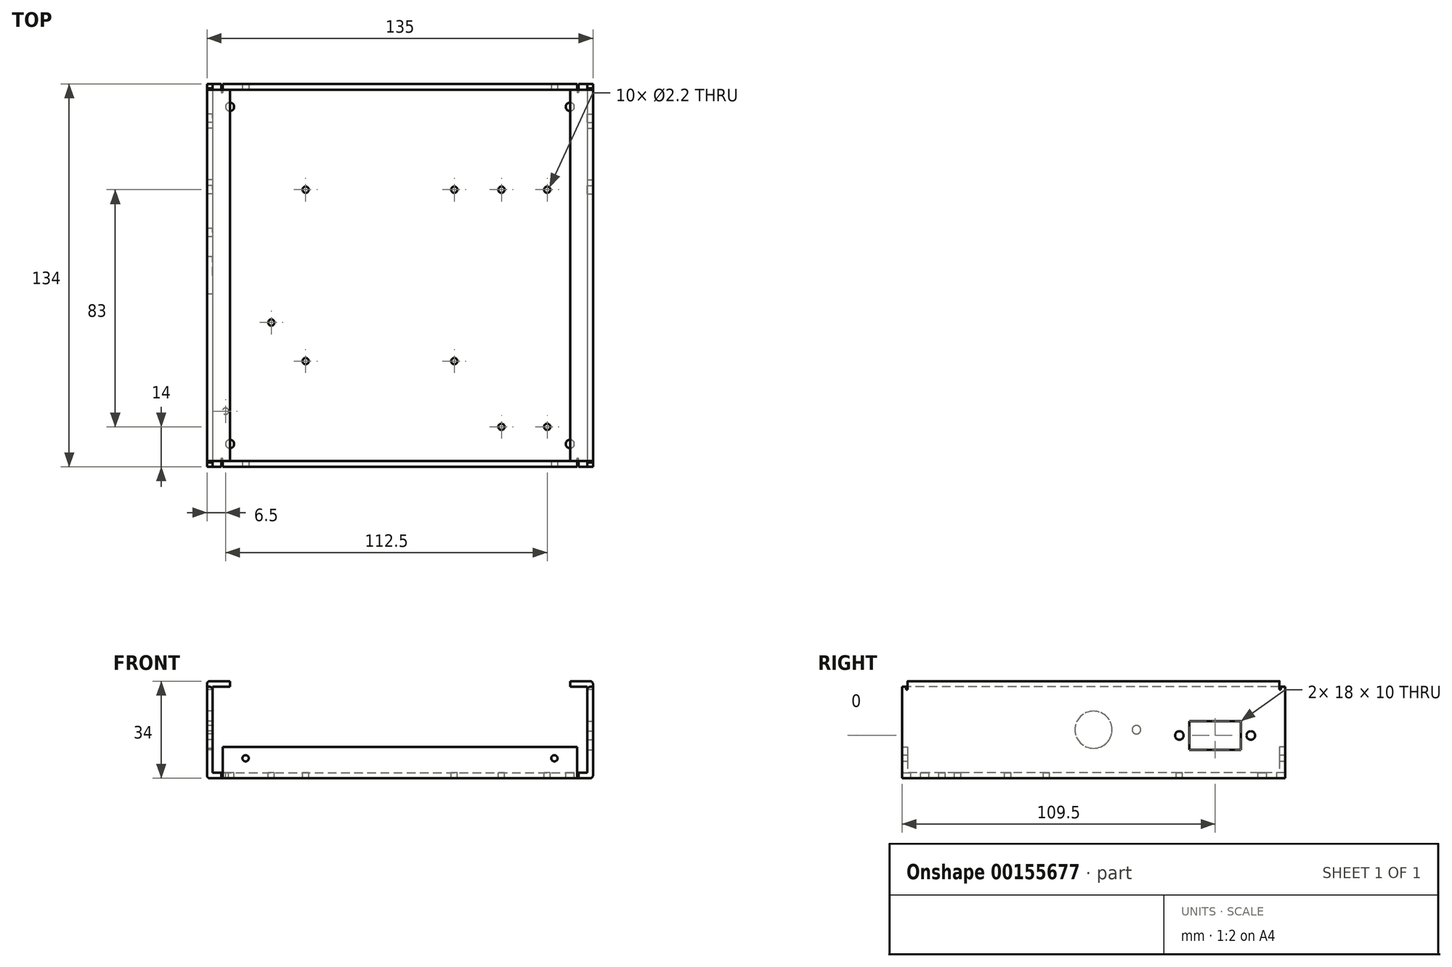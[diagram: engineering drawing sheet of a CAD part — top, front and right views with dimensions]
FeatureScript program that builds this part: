
annotation { "Feature Type Name" : "Feature", "Feature Type Description" : "" }
export const myFeature = defineFeature(function(context is Context, id is Id, definition is map)
    precondition{}
    {
        {
            var Q0;
            Q0=qCreatedBy(makeId("Top.planeOp"),FACE);
            var sketch = newSketch(context, id + "F0", { "sketchPlane" : qUnion([Q0])});
            skLineSegment(sketch, "E0.bottom", {"start": v(67.5, -67) * mm, "end": v(62.5, -67) * mm});
            skLineSegment(sketch, "E0.top", {"start": v(67.5, 67) * mm, "end": v(62.5, 67) * mm});
            skLineSegment(sketch, "E0.left", {"start": v(67.5, -67) * mm, "end": v(67.5, 67) * mm});
            skLineSegment(sketch, "E0.right", {"start": v(-67.5, -67) * mm, "end": v(-67.5, 67) * mm});
            skPoint(sketch, "E0.middle", {"position": v(0, 0) * mm});
            skLineSegment(sketch, "E1.top", {"start": v(-62.5, -64) * mm, "end": v(-62, -64) * mm});
            skLineSegment(sketch, "E1.left", {"start": v(-62.5, -67) * mm, "end": v(-62.5, -64) * mm});
            skLineSegment(sketch, "E1.right", {"start": v(-62, -67) * mm, "end": v(-62, -64) * mm});
            skLineSegment(sketch, "E2.trimOffspring", {"start": v(-62.5, -67) * mm, "end": v(-67.5, -67) * mm});
            skLineSegment(sketch, "E3.top", {"start": v(62, -64) * mm, "end": v(62.5, -64) * mm});
            skLineSegment(sketch, "E3.left", {"start": v(62, -67) * mm, "end": v(62, -64) * mm});
            skLineSegment(sketch, "E3.right", {"start": v(62.5, -67) * mm, "end": v(62.5, -64) * mm});
            skLineSegment(sketch, "E4.trimOffspring", {"start": v(62, -67) * mm, "end": v(-62, -67) * mm});
            skLineSegment(sketch, "E5.top", {"start": v(-62.5, 64) * mm, "end": v(-62, 64) * mm});
            skLineSegment(sketch, "E5.left", {"start": v(-62.5, 67) * mm, "end": v(-62.5, 64) * mm});
            skLineSegment(sketch, "E5.right", {"start": v(-62, 67) * mm, "end": v(-62, 64) * mm});
            skLineSegment(sketch, "E6.top", {"start": v(62.5, 64) * mm, "end": v(62, 64) * mm});
            skLineSegment(sketch, "E6.left", {"start": v(62.5, 67) * mm, "end": v(62.5, 64) * mm});
            skLineSegment(sketch, "E6.right", {"start": v(62, 67) * mm, "end": v(62, 64) * mm});
            skLineSegment(sketch, "E7.trimOffspring", {"start": v(-62.5, 67) * mm, "end": v(-67.5, 67) * mm});
            skLineSegment(sketch, "E8.trimOffspring", {"start": v(62, 67) * mm, "end": v(-62, 67) * mm});
            skSolve(sketch);
        }
        {
            var Q0;
            Q0 = qSketchRegion(id + "F0", true);
            extrude(context, id + "F1", {"entities" : qUnion([Q0]), "depth" : 2 * mm});
        }
        {
            var Q0;
            Q0=makeQuery(id+"F1.opExtrude","CAP_FACE",FACE,{"disambiguationData":[OSD([sQuery(id+"F0.wireOp",EDGE,"E0.bottom"),sQuery(id+"F0.wireOp",EDGE,"E0.top"),sQuery(id+"F0.wireOp",EDGE,"E0.left"),sQuery(id+"F0.wireOp",EDGE,"E0.right")])],"isStart":false});
            var sketch = newSketch(context, id + "F2", { "sketchPlane" : qUnion([Q0])});
            skLineSegment(sketch, "E9.bottom", {"start": v(67.5, 67) * mm, "end": v(65.5, 67) * mm});
            skLineSegment(sketch, "E9.top", {"start": v(67.5, -67) * mm, "end": v(65.5, -67) * mm});
            skLineSegment(sketch, "E9.left", {"start": v(67.5, 67) * mm, "end": v(67.5, -67) * mm});
            skLineSegment(sketch, "E9.right", {"start": v(65.5, 67) * mm, "end": v(65.5, -67) * mm});
            skLineSegment(sketch, "E10.bottom", {"start": v(-67.5, 67) * mm, "end": v(-65.5, 67) * mm});
            skLineSegment(sketch, "E10.top", {"start": v(-67.5, -67) * mm, "end": v(-65.5, -67) * mm});
            skLineSegment(sketch, "E10.left", {"start": v(-67.5, 67) * mm, "end": v(-67.5, -67) * mm});
            skLineSegment(sketch, "E10.right", {"start": v(-65.5, 67) * mm, "end": v(-65.5, -67) * mm});
            skSolve(sketch);
        }
        {
            var Q0;
            Q0 = qSketchRegion(id + "F2", true);
            extrude(context, id + "F3", {"entities" : qUnion([Q0]), "operationType" : NewBodyOperationType.ADD, "depth" : 30 * mm});
        }
        {
            var Q0;
            Q0=makeQuery(id+"F1.opExtrude","CAP_EDGE",EDGE,{"disambiguationData":[OSD([sQuery(id+"F0.wireOp",EDGE,"E0.right")])],"isStart":true});
            var Q1;
            Q1=makeQuery(id+"F1.opExtrude","CAP_EDGE",EDGE,{"disambiguationData":[OSD([sQuery(id+"F0.wireOp",EDGE,"E0.left")])],"isStart":true});
            var Q2;
            Q2=makeQuery(id+"F3.opExtrude","CAP_EDGE",EDGE,{"disambiguationData":[OSD([sQuery(id+"F2.wireOp",EDGE,"E10.right")])],"isStart":true});
            var Q3;
            Q3=makeQuery(id+"F3.opExtrude","CAP_EDGE",EDGE,{"disambiguationData":[OSD([sQuery(id+"F2.wireOp",EDGE,"E9.right")])],"isStart":true});
            fillet(context, id + "F4", {"entities" : qUnion([Q0, Q1, Q2, Q3]), "radius" : 1 * mm, "tangentPropagation" : true, "allowEdgeOverflow" : false});
        }
        {
            var Q0;
            Q0=makeQuery(id+"F3.opExtrude","CAP_FACE",FACE,{"disambiguationData":[OSD([sQuery(id+"F2.wireOp",EDGE,"E10.bottom"),sQuery(id+"F2.wireOp",EDGE,"E10.top"),sQuery(id+"F2.wireOp",EDGE,"E10.left"),sQuery(id+"F2.wireOp",EDGE,"E10.right")])],"isStart":false});
            var sketch = newSketch(context, id + "F5", { "sketchPlane" : qUnion([Q0])});
            skLineSegment(sketch, "E11.bottom", {"start": v(-67.5, 65) * mm, "end": v(-59.5, 65) * mm});
            skLineSegment(sketch, "E11.top", {"start": v(-67.5, -65) * mm, "end": v(-59.5, -65) * mm});
            skLineSegment(sketch, "E11.left", {"start": v(-67.5, 65) * mm, "end": v(-67.5, -65) * mm});
            skLineSegment(sketch, "E11.right", {"start": v(-59.5, 65) * mm, "end": v(-59.5, -65) * mm});
            skLineSegment(sketch, "E12.bottom", {"start": v(59.5, 65) * mm, "end": v(67.5, 65) * mm});
            skLineSegment(sketch, "E12.top", {"start": v(59.5, -65) * mm, "end": v(67.5, -65) * mm});
            skLineSegment(sketch, "E12.left", {"start": v(59.5, 65) * mm, "end": v(59.5, -65) * mm});
            skLineSegment(sketch, "E12.right", {"start": v(67.5, 65) * mm, "end": v(67.5, -65) * mm});
            skSolve(sketch);
        }
        {
            var Q0;
            Q0 = qSketchRegion(id + "F5", true);
            extrude(context, id + "F6", {"entities" : qUnion([Q0]), "operationType" : NewBodyOperationType.ADD, "depth" : 2 * mm});
        }
        {
            var Q0;
            Q0=makeQuery(id+"F6.opExtrude","CAP_EDGE",EDGE,{"disambiguationData":[OSD([sQuery(id+"F5.wireOp",EDGE,"E11.left")])],"isStart":false});
            var Q1;
            Q1=makeQuery(id+"F6.opExtrude","CAP_EDGE",EDGE,{"disambiguationData":[OSD([sQuery(id+"F5.wireOp",EDGE,"E12.right")])],"isStart":false});
            var Q2;
            {var subQ0=sQuery(id+"F5.wireOp",EDGE,"E11.top");var subQ1=sQuery(id+"F5.wireOp",EDGE,"E11.bottom");var subQ2=sQuery(id+"F2.wireOp",EDGE,"E10.right");Q2=makeQuery(id+"F6.boolean.opBoolean","SPLIT",EDGE,{"disambiguationData":[TD([makeQuery(id+"F3.opExtrude","CAP_FACE",FACE,{"disambiguationData":[OSD([sQuery(id+"F2.wireOp",EDGE,"E10.bottom"),sQuery(id+"F2.wireOp",EDGE,"E10.top"),sQuery(id+"F2.wireOp",EDGE,"E10.left"),subQ2])],"isStart":false}),makeQuery(id+"F3.opExtrude","SWEPT_FACE",FACE,{"disambiguationData":[OSD([subQ2])]}),makeQuery(id+"F6.opExtrude","SWEPT_FACE",FACE,{"disambiguationData":[OSD([subQ1])]}),makeQuery(id+"F6.opExtrude","CAP_FACE",FACE,{"disambiguationData":[OSD([subQ1,subQ0,sQuery(id+"F5.wireOp",EDGE,"E11.left"),sQuery(id+"F5.wireOp",EDGE,"E11.right")])],"isStart":true}),makeQuery(id+"F6.opExtrude","SWEPT_FACE",FACE,{"disambiguationData":[OSD([subQ0])]})])],"derivedFrom":makeQuery(id+"F3.opExtrude","CAP_EDGE",EDGE,{"disambiguationData":[OSD([subQ2])],"isStart":false})});}
            var Q3;
            {var subQ0=sQuery(id+"F5.wireOp",EDGE,"E12.top");var subQ1=sQuery(id+"F5.wireOp",EDGE,"E12.bottom");var subQ2=sQuery(id+"F2.wireOp",EDGE,"E9.right");Q3=makeQuery(id+"F6.boolean.opBoolean","SPLIT",EDGE,{"disambiguationData":[TD([makeQuery(id+"F3.opExtrude","CAP_FACE",FACE,{"disambiguationData":[OSD([sQuery(id+"F2.wireOp",EDGE,"E9.bottom"),sQuery(id+"F2.wireOp",EDGE,"E9.top"),sQuery(id+"F2.wireOp",EDGE,"E9.left"),subQ2])],"isStart":false}),makeQuery(id+"F3.opExtrude","SWEPT_FACE",FACE,{"disambiguationData":[OSD([subQ2])]}),makeQuery(id+"F6.opExtrude","SWEPT_FACE",FACE,{"disambiguationData":[OSD([subQ1])]}),makeQuery(id+"F6.opExtrude","CAP_FACE",FACE,{"disambiguationData":[OSD([subQ1,subQ0,sQuery(id+"F5.wireOp",EDGE,"E12.left"),sQuery(id+"F5.wireOp",EDGE,"E12.right")])],"isStart":true}),makeQuery(id+"F6.opExtrude","SWEPT_FACE",FACE,{"disambiguationData":[OSD([subQ0])]})])],"derivedFrom":makeQuery(id+"F3.opExtrude","CAP_EDGE",EDGE,{"disambiguationData":[OSD([subQ2])],"isStart":false})});}
            fillet(context, id + "F7", {"entities" : qUnion([Q0, Q1, Q2, Q3]), "radius" : 1 * mm, "tangentPropagation" : true, "allowEdgeOverflow" : false});
        }
        {
            var Q0;
            Q0=makeQuery(id+"F1.opExtrude","CAP_FACE",FACE,{"disambiguationData":[OSD([sQuery(id+"F0.wireOp",EDGE,"E0.bottom"),sQuery(id+"F0.wireOp",EDGE,"E0.top"),sQuery(id+"F0.wireOp",EDGE,"E0.left"),sQuery(id+"F0.wireOp",EDGE,"E0.right"),sQuery(id+"F0.wireOp",EDGE,"E1.top"),sQuery(id+"F0.wireOp",EDGE,"E1.left"),sQuery(id+"F0.wireOp",EDGE,"E1.right"),sQuery(id+"F0.wireOp",EDGE,"E2.trimOffspring"),sQuery(id+"F0.wireOp",EDGE,"E3.top"),sQuery(id+"F0.wireOp",EDGE,"E3.left"),sQuery(id+"F0.wireOp",EDGE,"E3.right"),sQuery(id+"F0.wireOp",EDGE,"E4.trimOffspring")])],"isStart":false});
            var sketch = newSketch(context, id + "F8", { "sketchPlane" : qUnion([Q0])});
            skLineSegment(sketch, "E13.bottom", {"start": v(-62, -65) * mm, "end": v(62, -65) * mm});
            skLineSegment(sketch, "E13.top", {"start": v(-62, -67) * mm, "end": v(62, -67) * mm});
            skLineSegment(sketch, "E13.left", {"start": v(-62, -65) * mm, "end": v(-62, -67) * mm});
            skLineSegment(sketch, "E13.right", {"start": v(62, -65) * mm, "end": v(62, -67) * mm});
            skLineSegment(sketch, "E14.bottom", {"start": v(-62, 67) * mm, "end": v(62, 67) * mm});
            skLineSegment(sketch, "E14.top", {"start": v(-62, 65) * mm, "end": v(62, 65) * mm});
            skLineSegment(sketch, "E14.left", {"start": v(-62, 67) * mm, "end": v(-62, 65) * mm});
            skLineSegment(sketch, "E14.right", {"start": v(62, 67) * mm, "end": v(62, 65) * mm});
            skSolve(sketch);
        }
        {
            var Q0;
            Q0 = qSketchRegion(id + "F8", true);
            extrude(context, id + "F9", {"entities" : qUnion([Q0]), "operationType" : NewBodyOperationType.ADD, "depth" : 9 * mm});
        }
        {
            var Q0;
            Q0=makeQuery(id+"F1.opExtrude","CAP_EDGE",EDGE,{"disambiguationData":[OSD([sQuery(id+"F0.wireOp",EDGE,"E4.trimOffspring")])],"isStart":true});
            var Q1;
            Q1=makeQuery(id+"F9.opExtrude","CAP_EDGE",EDGE,{"disambiguationData":[OSD([sQuery(id+"F8.wireOp",EDGE,"E13.bottom")])],"isStart":true});
            var Q2;
            Q2=makeQuery(id+"F9.opExtrude","CAP_EDGE",EDGE,{"disambiguationData":[OSD([sQuery(id+"F8.wireOp",EDGE,"E14.top")])],"isStart":true});
            var Q3;
            Q3=makeQuery(id+"F1.opExtrude","CAP_EDGE",EDGE,{"disambiguationData":[OSD([sQuery(id+"F0.wireOp",EDGE,"E8.trimOffspring")])],"isStart":true});
            fillet(context, id + "F10", {"entities" : qUnion([Q0, Q1, Q2, Q3]), "radius" : 1 * mm, "tangentPropagation" : true, "allowEdgeOverflow" : false});
        }
        {
            var Q0;
            Q0=makeQuery(id+"F6.boolean.opBoolean","MERGE",FACE,{"derivedFrom":[makeQuery(id+"F3.boolean.opBoolean","MERGE",FACE,{"derivedFrom":[makeQuery(id+"F1.opExtrude","SWEPT_FACE",FACE,{"disambiguationData":[OSD([sQuery(id+"F0.wireOp",EDGE,"E0.right")])]}),makeQuery(id+"F3.opExtrude","SWEPT_FACE",FACE,{"disambiguationData":[OSD([sQuery(id+"F2.wireOp",EDGE,"LtGDmYED-3yVl-KpR6-pZyB-YukeFVbaKuZ8.left")])]})]}),makeQuery(id+"F6.opExtrude","SWEPT_FACE",FACE,{"disambiguationData":[OSD([sQuery(id+"F5.wireOp",EDGE,"E11.left")])]})]});
            var sketch = newSketch(context, id + "F11", { "sketchPlane" : qUnion([Q0])});
            skLineSegment(sketch, "E15.bottom", {"start": v(65, 32) * mm, "end": v(65.5, 32) * mm});
            skLineSegment(sketch, "E15.top", {"start": v(65, 31) * mm, "end": v(65.5, 31) * mm});
            skLineSegment(sketch, "E15.left", {"start": v(65, 32) * mm, "end": v(65, 31) * mm});
            skLineSegment(sketch, "E15.right", {"start": v(65.5, 32) * mm, "end": v(65.5, 31) * mm});
            skLineSegment(sketch, "E16.bottom", {"start": v(-65, 32) * mm, "end": v(-65.5, 32) * mm});
            skLineSegment(sketch, "E16.top", {"start": v(-65, 31) * mm, "end": v(-65.5, 31) * mm});
            skLineSegment(sketch, "E16.left", {"start": v(-65, 32) * mm, "end": v(-65, 31) * mm});
            skLineSegment(sketch, "E16.right", {"start": v(-65.5, 32) * mm, "end": v(-65.5, 31) * mm});
            skSolve(sketch);
        }
        {
            var Q0;
            Q0 = qSketchRegion(id + "F11", true);
            extrude(context, id + "F12", {"entities" : qUnion([Q0]), "operationType" : NewBodyOperationType.REMOVE, "endBound" : BoundingType.THROUGH_ALL, "oppositeDirection" : true, "depth" : 25 * mm});
        }
        {
            var Q0;
            Q0=makeQuery(id+"F6.boolean.opBoolean","MERGE",FACE,{"derivedFrom":[makeQuery(id+"F3.boolean.opBoolean","MERGE",FACE,{"derivedFrom":[makeQuery(id+"F1.opExtrude","SWEPT_FACE",FACE,{"disambiguationData":[OSD([sQuery(id+"F0.wireOp",EDGE,"E0.right")])]}),makeQuery(id+"F3.opExtrude","SWEPT_FACE",FACE,{"disambiguationData":[OSD([sQuery(id+"F2.wireOp",EDGE,"E10.left")])]})]}),makeQuery(id+"F6.opExtrude","SWEPT_FACE",FACE,{"disambiguationData":[OSD([sQuery(id+"F5.wireOp",EDGE,"E11.left")])]})]});
            var sketch = newSketch(context, id + "F13", { "sketchPlane" : qUnion([Q0])});
            skCircle(sketch, "E17", {"center": v(-55, 15) * mm, "radius": 1.5 * mm});
            skCircle(sketch, "E18", {"center": v(-30, 15) * mm, "radius": 1.5 * mm});
            skCircle(sketch, "E19", {"center": v(0, 17) * mm, "radius": 6.5 * mm});
            skCircle(sketch, "E20", {"center": v(-15, 17) * mm, "radius": 1.5 * mm});
            skLineSegment(sketch, "E21.bottom", {"start": v(-33.5, 10) * mm, "end": v(-51.5, 10) * mm});
            skLineSegment(sketch, "E21.top", {"start": v(-33.5, 20) * mm, "end": v(-51.5, 20) * mm});
            skLineSegment(sketch, "E21.left", {"start": v(-33.5, 10) * mm, "end": v(-33.5, 20) * mm});
            skLineSegment(sketch, "E21.right", {"start": v(-51.5, 10) * mm, "end": v(-51.5, 20) * mm});
            skPoint(sketch, "E21.middle", {"position": v(-42.5, 15) * mm});
            skSolve(sketch);
        }
        {
            var Q0;
            Q0 = qSketchRegion(id + "F13", true);
            extrude(context, id + "F14", {"entities" : qUnion([Q0]), "operationType" : NewBodyOperationType.REMOVE, "oppositeDirection" : true, "depth" : 3 * mm});
        }
        {
            var Q0;
            Q0=makeQuery(id+"F1.opExtrude","CAP_FACE",FACE,{"disambiguationData":[OSD([sQuery(id+"F0.wireOp",EDGE,"E0.bottom"),sQuery(id+"F0.wireOp",EDGE,"E0.top"),sQuery(id+"F0.wireOp",EDGE,"E0.left"),sQuery(id+"F0.wireOp",EDGE,"E0.right"),sQuery(id+"F0.wireOp",EDGE,"E1.top"),sQuery(id+"F0.wireOp",EDGE,"E1.left"),sQuery(id+"F0.wireOp",EDGE,"E1.right"),sQuery(id+"F0.wireOp",EDGE,"E2.trimOffspring"),sQuery(id+"F0.wireOp",EDGE,"E3.top"),sQuery(id+"F0.wireOp",EDGE,"E3.left"),sQuery(id+"F0.wireOp",EDGE,"E3.right"),sQuery(id+"F0.wireOp",EDGE,"E4.trimOffspring"),sQuery(id+"F0.wireOp",EDGE,"E5.top"),sQuery(id+"F0.wireOp",EDGE,"E5.left"),sQuery(id+"F0.wireOp",EDGE,"E5.right"),sQuery(id+"F0.wireOp",EDGE,"E6.top"),sQuery(id+"F0.wireOp",EDGE,"E6.left"),sQuery(id+"F0.wireOp",EDGE,"E6.right"),sQuery(id+"F0.wireOp",EDGE,"E7.trimOffspring"),sQuery(id+"F0.wireOp",EDGE,"E8.trimOffspring")])],"isStart":false});
            var sketch = newSketch(context, id + "F15", { "sketchPlane" : qUnion([Q0])});
            skCircle(sketch, "E22", {"center": v(-33, 30) * mm, "radius": 1.1 * mm});
            skCircle(sketch, "E23", {"center": v(19, 30) * mm, "radius": 1.1 * mm});
            skCircle(sketch, "E24", {"center": v(-33, -30) * mm, "radius": 1.1 * mm});
            skCircle(sketch, "E25", {"center": v(19, -30) * mm, "radius": 1.1 * mm});
            skCircle(sketch, "E26", {"center": v(-45, -16.5) * mm, "radius": 1.1 * mm});
            skCircle(sketch, "E27", {"center": v(-61, -47.5) * mm, "radius": 1.1 * mm});
            skCircle(sketch, "E28", {"center": v(-59.5, 59) * mm, "radius": 1.5 * mm});
            skCircle(sketch, "E29", {"center": v(59.5, 59) * mm, "radius": 1.5 * mm});
            skCircle(sketch, "E30", {"center": v(-59.5, -59) * mm, "radius": 1.5 * mm});
            skCircle(sketch, "E31", {"center": v(59.5, -59) * mm, "radius": 1.5 * mm});
            skCircle(sketch, "E32", {"center": v(35.5, 30) * mm, "radius": 1.1 * mm});
            skCircle(sketch, "E33", {"center": v(51.5, 30) * mm, "radius": 1.1 * mm});
            skCircle(sketch, "E34", {"center": v(35.5, -53) * mm, "radius": 1.1 * mm});
            skCircle(sketch, "E35", {"center": v(51.5, -53) * mm, "radius": 1.1 * mm});
            skSolve(sketch);
        }
        {
            var Q0;
            Q0 = qSketchRegion(id + "F15", true);
            extrude(context, id + "F16", {"entities" : qUnion([Q0]), "operationType" : NewBodyOperationType.REMOVE, "oppositeDirection" : true, "depth" : 3 * mm});
        }
        {
            var Q0;
            Q0=makeQuery(id+"F9.boolean.opBoolean","MERGE",FACE,{"derivedFrom":[makeQuery(id+"F1.opExtrude","SWEPT_FACE",FACE,{"disambiguationData":[OSD([sQuery(id+"F0.wireOp",EDGE,"E4.trimOffspring")])]}),makeQuery(id+"F9.opExtrude","SWEPT_FACE",FACE,{"disambiguationData":[OSD([sQuery(id+"F8.wireOp",EDGE,"E13.top")])]})]});
            var sketch = newSketch(context, id + "F17", { "sketchPlane" : qUnion([Q0])});
            skCircle(sketch, "E36", {"center": v(54, 7) * mm, "radius": 1.1 * mm});
            skCircle(sketch, "E37", {"center": v(-54, 7) * mm, "radius": 1.1 * mm});
            skSolve(sketch);
        }
        {
            var Q0;
            Q0 = qSketchRegion(id + "F17", true);
            extrude(context, id + "F18", {"entities" : qUnion([Q0]), "operationType" : NewBodyOperationType.REMOVE, "endBound" : BoundingType.THROUGH_ALL, "oppositeDirection" : true, "depth" : 25 * mm});
        }
        {
            var Q0;
            Q0=makeQuery(id+"F6.boolean.opBoolean","MERGE",FACE,{"derivedFrom":[makeQuery(id+"F3.boolean.opBoolean","MERGE",FACE,{"derivedFrom":[makeQuery(id+"F1.opExtrude","SWEPT_FACE",FACE,{"disambiguationData":[OSD([sQuery(id+"F0.wireOp",EDGE,"E0.left")])]}),makeQuery(id+"F3.opExtrude","SWEPT_FACE",FACE,{"disambiguationData":[OSD([sQuery(id+"F2.wireOp",EDGE,"E9.left")])]})]}),makeQuery(id+"F6.opExtrude","SWEPT_FACE",FACE,{"disambiguationData":[OSD([sQuery(id+"F5.wireOp",EDGE,"E12.right")])]})]});
            var sketch = newSketch(context, id + "F19", { "sketchPlane" : qUnion([Q0])});
            skCircle(sketch, "E38", {"center": v(30, 15) * mm, "radius": 1.5 * mm});
            skCircle(sketch, "E39", {"center": v(55, 15) * mm, "radius": 1.5 * mm});
            skLineSegment(sketch, "E40.bottom", {"start": v(51.5, 10) * mm, "end": v(33.5, 10) * mm});
            skLineSegment(sketch, "E40.top", {"start": v(51.5, 20) * mm, "end": v(33.5, 20) * mm});
            skLineSegment(sketch, "E40.left", {"start": v(51.5, 10) * mm, "end": v(51.5, 20) * mm});
            skLineSegment(sketch, "E40.right", {"start": v(33.5, 10) * mm, "end": v(33.5, 20) * mm});
            skPoint(sketch, "E40.middle", {"position": v(42.5, 15) * mm});
            skSolve(sketch);
        }
        {
            var Q0;
            Q0 = qSketchRegion(id + "F19", true);
            extrude(context, id + "F20", {"entities" : qUnion([Q0]), "operationType" : NewBodyOperationType.REMOVE, "oppositeDirection" : true, "depth" : 3 * mm});
        }
    });
